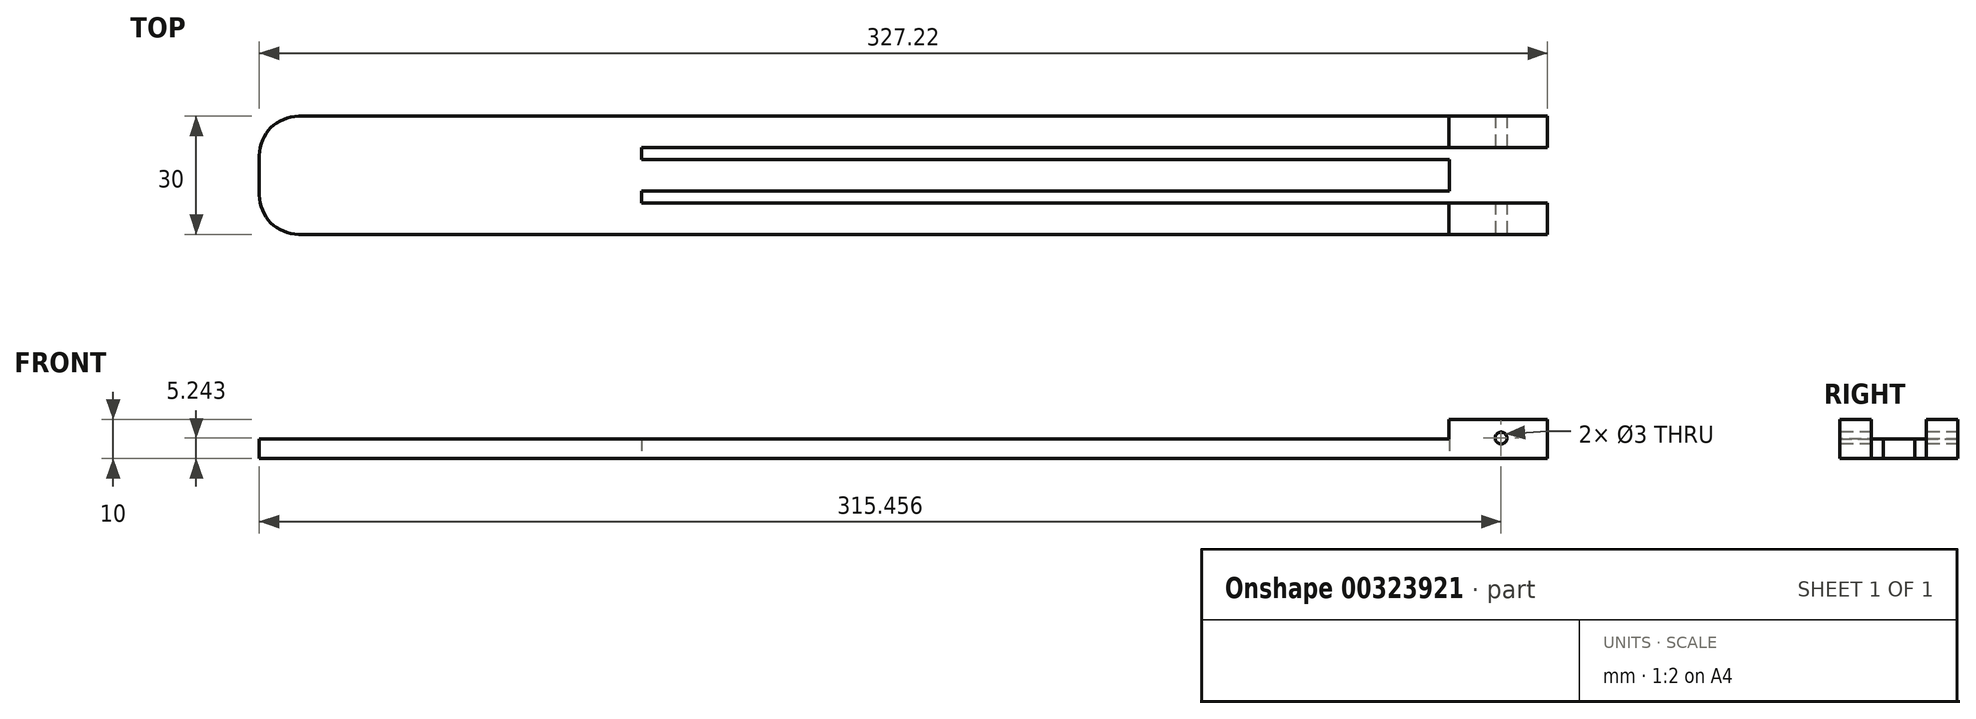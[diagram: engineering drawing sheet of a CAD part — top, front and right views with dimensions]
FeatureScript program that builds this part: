
annotation { "Feature Type Name" : "Feature", "Feature Type Description" : "" }
export const myFeature = defineFeature(function(context is Context, id is Id, definition is map)
    precondition{}
    {
        {
            var Q0;
            Q0=qCreatedBy(makeId("Top.planeOp"),FACE);
            var sketch = newSketch(context, id + "F0", { "sketchPlane" : qUnion([Q0])});
            skLineSegment(sketch, "E0.bottom", {"start": v(163.6, -15) * mm, "end": v(-153.6, -15) * mm});
            skLineSegment(sketch, "E0.top", {"start": v(163.6, 15) * mm, "end": v(-153.6, 15) * mm});
            skLineSegment(sketch, "E0.left", {"start": v(163.6, -15) * mm, "end": v(163.6, -7) * mm});
            skLineSegment(sketch, "E0.right", {"start": v(-163.6, -5) * mm, "end": v(-163.6, 5) * mm});
            skPoint(sketch, "E0.middle", {"position": v(0, 0) * mm});
            skLineSegment(sketch, "E1.bottom", {"start": v(163.6, 7) * mm, "end": v(-66.56, 7) * mm});
            skLineSegment(sketch, "E1.top", {"start": v(138.75, 4) * mm, "end": v(-66.56, 4) * mm});
            skLineSegment(sketch, "E1.right", {"start": v(-66.56, 7) * mm, "end": v(-66.56, 4) * mm});
            skLineSegment(sketch, "E2.bottom", {"start": v(138.75, -4) * mm, "end": v(-66.56, -4) * mm});
            skLineSegment(sketch, "E2.top", {"start": v(163.6, -7) * mm, "end": v(-66.56, -7) * mm});
            skLineSegment(sketch, "E2.right", {"start": v(-66.56, -4) * mm, "end": v(-66.56, -7) * mm});
            skLineSegment(sketch, "E3.trimOffspring", {"start": v(163.6, 7) * mm, "end": v(163.6, 15) * mm});
            skLineSegment(sketch, "E4.left", {"start": v(138.75, -4) * mm, "end": v(138.75, 4) * mm});
            skPoint(sketch, "E5.visualSharp", {"position": v(-163.6, 15) * mm});
            skArc(sketch, "E5.filletArc", {"start": v(-153.6, 15) * mm, "mid": v(-160.68, 12.07) * mm, "end": v(-163.6, 5) * mm});
            skPoint(sketch, "E6.visualSharp", {"position": v(-163.6, -15) * mm});
            skArc(sketch, "E6.filletArc", {"start": v(-163.6, -5) * mm, "mid": v(-160.68, -12.07) * mm, "end": v(-153.6, -15) * mm});
            skSolve(sketch);
        }
        {
            var Q0;
            Q0 = qSketchRegion(id + "F0", true);
            extrude(context, id + "F1", {"entities" : qUnion([Q0]), "depth" : 5 * mm});
        }
        {
            var Q0;
            Q0=makeQuery(id+"F1.opExtrude","CAP_FACE",FACE,{"disambiguationData":[OSD([sQuery(id+"F0.wireOp",EDGE,"E0.bottom"),sQuery(id+"F0.wireOp",EDGE,"E0.top"),sQuery(id+"F0.wireOp",EDGE,"E0.left"),sQuery(id+"F0.wireOp",EDGE,"E0.right"),sQuery(id+"F0.wireOp",EDGE,"E1.bottom"),sQuery(id+"F0.wireOp",EDGE,"E1.top"),sQuery(id+"F0.wireOp",EDGE,"E1.right"),sQuery(id+"F0.wireOp",EDGE,"E2.bottom"),sQuery(id+"F0.wireOp",EDGE,"E2.top"),sQuery(id+"F0.wireOp",EDGE,"E2.right"),sQuery(id+"F0.wireOp",EDGE,"E3.trimOffspring"),sQuery(id+"F0.wireOp",EDGE,"E4.left"),sQuery(id+"F0.wireOp",EDGE,"E5.filletArc"),sQuery(id+"F0.wireOp",EDGE,"E6.filletArc")])],"isStart":false});
            var sketch = newSketch(context, id + "F2", { "sketchPlane" : qUnion([Q0])});
            skLineSegment(sketch, "E7.bottom", {"start": v(163.6, -15) * mm, "end": v(138.6, -15) * mm});
            skLineSegment(sketch, "E7.top", {"start": v(163.6, -7) * mm, "end": v(138.6, -7) * mm});
            skLineSegment(sketch, "E7.left", {"start": v(163.6, -15) * mm, "end": v(163.6, -7) * mm});
            skLineSegment(sketch, "E7.right", {"start": v(138.6, -15) * mm, "end": v(138.6, -7) * mm});
            skLineSegment(sketch, "E8.bottom", {"start": v(163.6, 7) * mm, "end": v(138.6, 7) * mm});
            skLineSegment(sketch, "E8.top", {"start": v(163.6, 15) * mm, "end": v(138.6, 15) * mm});
            skLineSegment(sketch, "E8.left", {"start": v(163.6, 7) * mm, "end": v(163.6, 15) * mm});
            skLineSegment(sketch, "E8.right", {"start": v(138.6, 7) * mm, "end": v(138.6, 15) * mm});
            skSolve(sketch);
        }
        {
            var Q0;
            Q0=makeQuery(id+"F2.imprint","IMPRINT",FACE,{"disambiguationData":[TD([[makeQuery(id+"F2.imprint","IMPRINT",EDGE,{"derivedFrom":sQuery(id+"F2.wireOp",EDGE,"E7.bottom")}),-1.0]])]});
            var Q1;
            Q1=makeQuery(id+"F2.imprint","IMPRINT",FACE,{"disambiguationData":[TD([[makeQuery(id+"F2.imprint","IMPRINT",EDGE,{"derivedFrom":sQuery(id+"F2.wireOp",EDGE,"E8.bottom")}),-1.0]])]});
            extrude(context, id + "F3", {"entities" : qUnion([Q0, Q1]), "operationType" : NewBodyOperationType.ADD, "depth" : 5 * mm});
        }
        {
            var Q0;
            Q0=makeQuery(id+"F3.boolean.opBoolean","MERGE",FACE,{"derivedFrom":[makeQuery(id+"F1.opExtrude","SWEPT_FACE",FACE,{"disambiguationData":[OSD([sQuery(id+"F0.wireOp",EDGE,"E0.bottom")])]}),makeQuery(id+"F3.opExtrude","SWEPT_FACE",FACE,{"disambiguationData":[OSD([sQuery(id+"F2.wireOp",EDGE,"E7.bottom")])]})]});
            var sketch = newSketch(context, id + "F4", { "sketchPlane" : qUnion([Q0])});
            skCircle(sketch, "E9", {"center": v(151.85, 5.24) * mm, "radius": 1.5 * mm});
            skSolve(sketch);
        }
        {
            var Q0;
            Q0 = qSketchRegion(id + "F4", true);
            extrude(context, id + "F5", {"entities" : qUnion([Q0]), "operationType" : NewBodyOperationType.REMOVE, "oppositeDirection" : true, "depth" : 30.3 * mm});
        }
    });
